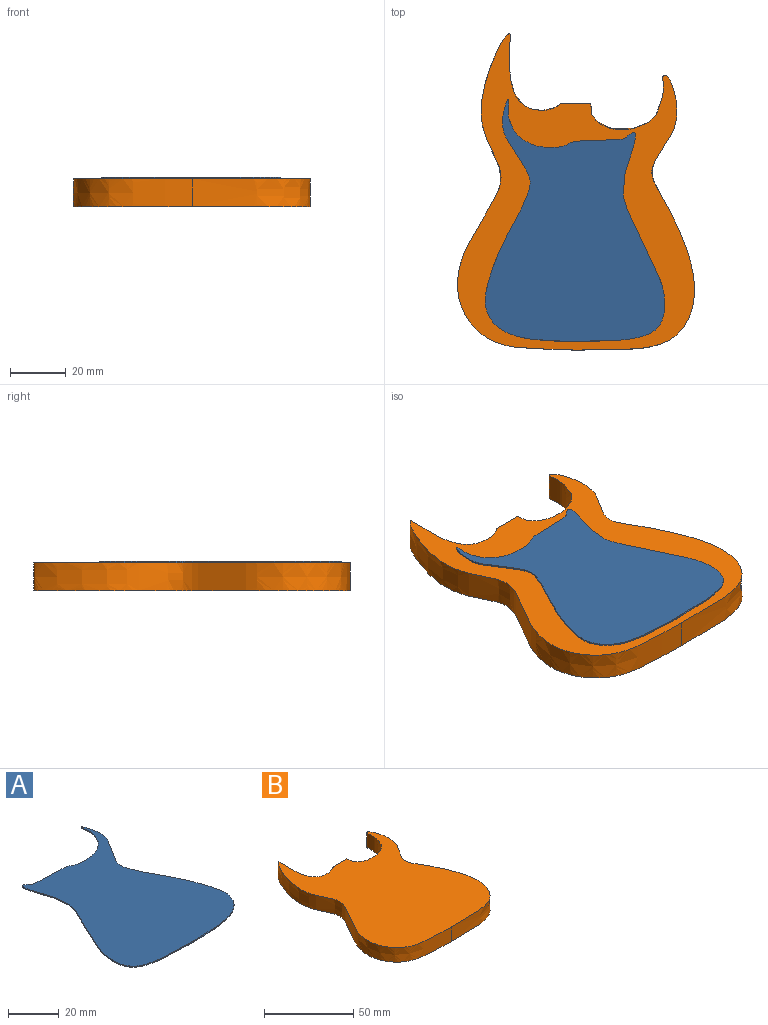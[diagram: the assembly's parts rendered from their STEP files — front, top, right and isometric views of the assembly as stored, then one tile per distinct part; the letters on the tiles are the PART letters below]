
ASSEMBLY  parts=2 mates=1
PART A: 3 faces, bbox 65.3x87.3x0.5 mm
  f0: extruded ~86.52x63.78mm, area 136.6mm2, adj f1,f2
  f1: plane 87.25x65.28mm, normal (0,0,1), area 3487.2mm2, adj f0
  f2: plane 87.25x65.28mm, normal (0,0,-1), area 3487.2mm2, adj f0
PART B: 10 faces, bbox 85.7x114.6x10 mm
  f0: extruded ~26.87x10mm, area 307.2mm2, adj f1,f7,f8,f9
  f1: extruded ~112.91x42.48mm, area 1523.8mm2, adj f0,f2,f8,f9
  f2: extruded ~98.34x42.15mm, area 1528.1mm2, adj f1,f3,f8,f9
  f3: extruded ~10x0.04mm, area 0.4mm2, adj f2,f4,f8,f9
  f4: extruded ~22.86x10mm, area 261.7mm2, adj f3,f5,f8,f9
  f5: extruded ~10x3.87mm, area 38.9mm2, adj f4,f6,f8,f9
  f6: plane 10.82x10mm, normal (0,1,0), area 108.2mm2, adj f5,f7,f8,f9
  f7: extruded ~10x9.52mm, area 100.9mm2, adj f0,f6,f8,f9
  f8: plane 114.57x85.73mm, normal (0,0,1), area 6167.4mm2, adj f0,f1,f2,f3,f4,f5,f6,f7
  f9: plane 114.57x85.73mm, normal (0,0,-1), area 6167.4mm2, adj f0,f1,f2,f3,f4,f5,f6,f7
PLACE A rot(axis=(0,1,0),180deg) t=(-29.95,-11.58,21.27)mm
PLACE B t=(-37.88,-6.96,0.77)mm
MATE fastened A.f1 <-> B.f8  axis (0,0,-1) through (-38.53,-41.01,10.77)mm
